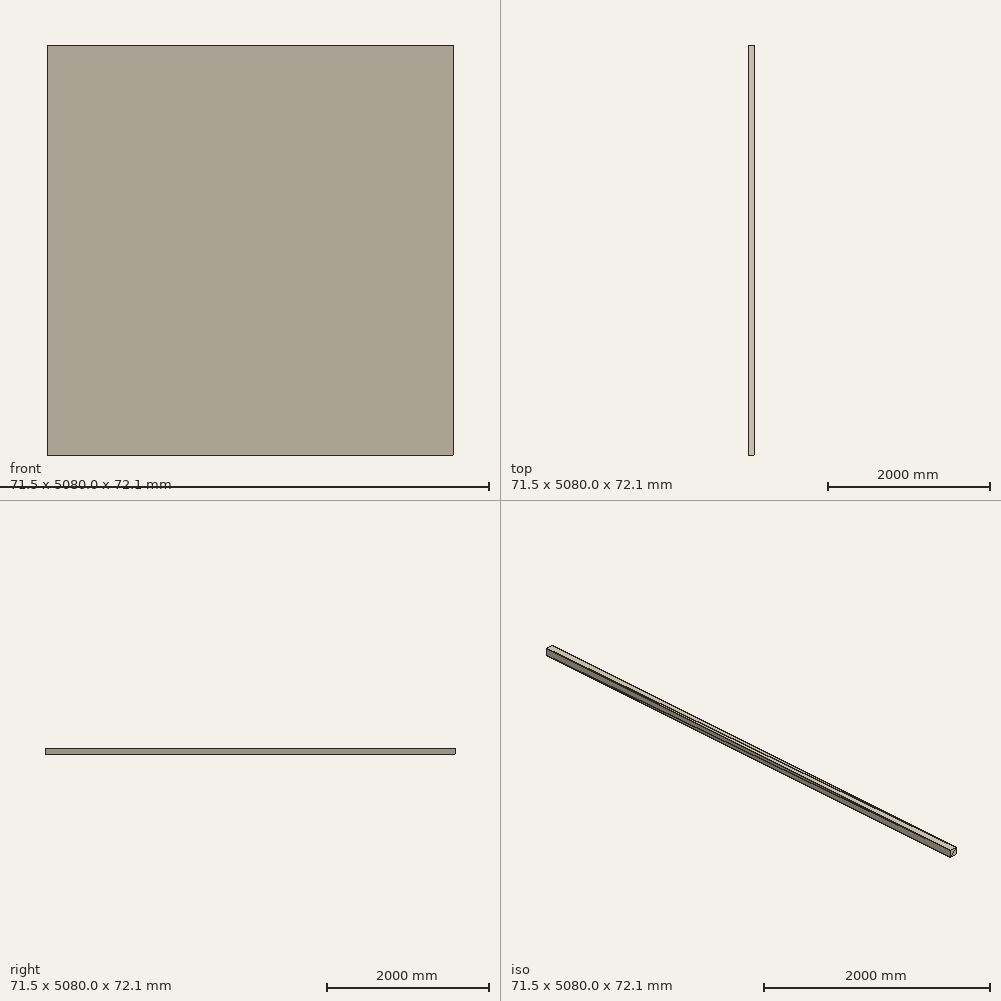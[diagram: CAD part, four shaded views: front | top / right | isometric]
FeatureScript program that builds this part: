
annotation { "Feature Type Name" : "Feature", "Feature Type Description" : "" }
export const myFeature = defineFeature(function(context is Context, id is Id, definition is map)
    precondition{}
    {
        {
            var Q0;
            Q0=qCreatedBy(makeId("Front.planeOp"),FACE);
            var sketch = newSketch(context, id + "F0", { "sketchPlane" : qUnion([Q0])});
            skLineSegment(sketch, "E0.bottom", {"start": v(-32.56, 38.7) * mm, "end": v(38.98, 38.7) * mm});
            skLineSegment(sketch, "E0.top", {"start": v(-32.56, -33.43) * mm, "end": v(38.98, -33.43) * mm});
            skLineSegment(sketch, "E0.left", {"start": v(-32.56, 38.7) * mm, "end": v(-32.56, -33.43) * mm});
            skLineSegment(sketch, "E0.right", {"start": v(38.98, 38.7) * mm, "end": v(38.98, -33.43) * mm});
            skSolve(sketch);
        }
        {
            var Q0;
            Q0=makeQuery(id+"F0.imprint","IMPRINT",FACE,{"disambiguationData":[TD([[makeQuery(id+"F0.imprint","IMPRINT",EDGE,{"derivedFrom":sQuery(id+"F0.wireOp",EDGE,"E0.bottom")}),-1.0]])]});
            extrude(context, id + "F1", {"entities" : qUnion([Q0]), "depth" : 5080 * mm, "offsetDistance" : 25.4 * mm});
        }
    });
